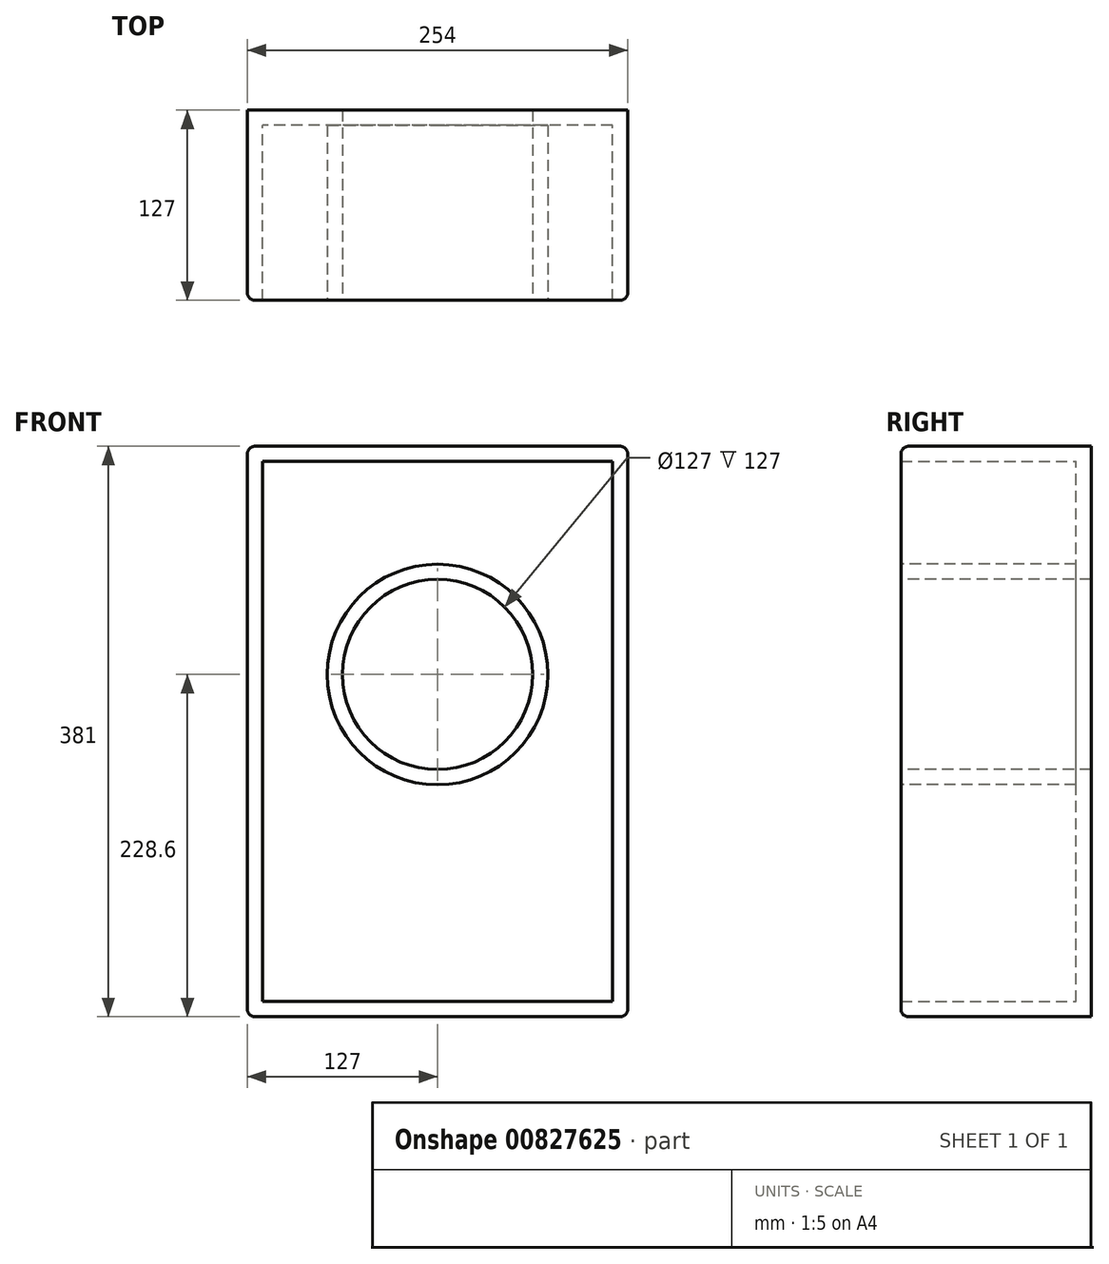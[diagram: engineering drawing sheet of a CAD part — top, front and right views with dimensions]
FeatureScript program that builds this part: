
annotation { "Feature Type Name" : "Feature", "Feature Type Description" : "" }
export const myFeature = defineFeature(function(context is Context, id is Id, definition is map)
    precondition{}
    {
        {
            var Q0;
            Q0=qCreatedBy(makeId("Front.planeOp"),FACE);
            var sketch = newSketch(context, id + "F0", { "sketchPlane" : qUnion([Q0])});
            skLineSegment(sketch, "E0.bottom", {"start": v(127, -190.5) * mm, "end": v(-127, -190.5) * mm});
            skLineSegment(sketch, "E0.top", {"start": v(127, 190.5) * mm, "end": v(-127, 190.5) * mm});
            skLineSegment(sketch, "E0.left", {"start": v(127, -190.5) * mm, "end": v(127, 190.5) * mm});
            skLineSegment(sketch, "E0.right", {"start": v(-127, -190.5) * mm, "end": v(-127, 190.5) * mm});
            skPoint(sketch, "E0.middle", {"position": v(0, 0) * mm});
            skSolve(sketch);
        }
        {
            var Q0;
            Q0=makeQuery(id+"F0.imprint","IMPRINT",FACE,{"disambiguationData":[TD([[makeQuery(id+"F0.imprint","IMPRINT",EDGE,{"derivedFrom":sQuery(id+"F0.wireOp",EDGE,"E0.bottom")}),-1.0]])]});
            extrude(context, id + "F1", {"entities" : qUnion([Q0]), "depth" : 127 * mm, "offsetDistance" : 25.4 * mm});
        }
        {
            var Q0;
            Q0=makeQuery(id+"F1.opExtrude","CAP_FACE",FACE,{"disambiguationData":[OSD([sQuery(id+"F0.wireOp",EDGE,"E0.bottom"),sQuery(id+"F0.wireOp",EDGE,"E0.top"),sQuery(id+"F0.wireOp",EDGE,"E0.left"),sQuery(id+"F0.wireOp",EDGE,"E0.right")])],"isStart":false});
            var sketch = newSketch(context, id + "F2", { "sketchPlane" : qUnion([Q0])});
            skCircle(sketch, "E1", {"center": v(0, 38.1) * mm, "radius": 63.5 * mm});
            skSolve(sketch);
        }
        {
            var Q0;
            Q0=makeQuery(id+"F2.imprint","IMPRINT",FACE,{"disambiguationData":[TD([[makeQuery(id+"F2.imprint","IMPRINT",EDGE,{"derivedFrom":sQuery(id+"F2.wireOp",EDGE,"E1")}),1.0]])]});
            var Q1;
            Q1=sQuery(id+"F2.wireOp",EDGE,"E1");
            extrude(context, id + "F3", {"entities" : qUnion([Q0]), "operationType" : NewBodyOperationType.REMOVE, "surfaceEntities" : qUnion([Q1]), "endBound" : BoundingType.THROUGH_ALL, "oppositeDirection" : true, "depth" : 25.4 * mm, "offsetDistance" : 25.4 * mm});
        }
        {
            var Q0;
            Q0=makeQuery(id+"F1.opExtrude","CAP_FACE",FACE,{"disambiguationData":[OSD([sQuery(id+"F0.wireOp",EDGE,"E0.bottom"),sQuery(id+"F0.wireOp",EDGE,"E0.top"),sQuery(id+"F0.wireOp",EDGE,"E0.left"),sQuery(id+"F0.wireOp",EDGE,"E0.right")])],"isStart":false});
            shell(context, id + "F4", {"entities" : qUnion([Q0]), "thickness" : 10.16 * mm});
        }
        {
            var Q0;
            Q0=makeQuery(id+"F1.opExtrude","CAP_EDGE",EDGE,{"disambiguationData":[OSD([sQuery(id+"F0.wireOp",EDGE,"E0.right")])],"isStart":false});
            var Q1;
            Q1=makeQuery(id+"F1.opExtrude","CAP_EDGE",EDGE,{"disambiguationData":[OSD([sQuery(id+"F0.wireOp",EDGE,"E0.top")])],"isStart":false});
            var Q2;
            Q2=makeQuery(id+"F1.opExtrude","CAP_EDGE",EDGE,{"disambiguationData":[OSD([sQuery(id+"F0.wireOp",EDGE,"E0.left")])],"isStart":false});
            var Q3;
            Q3=makeQuery(id+"F1.opExtrude","CAP_EDGE",EDGE,{"disambiguationData":[OSD([sQuery(id+"F0.wireOp",EDGE,"E0.bottom")])],"isStart":false});
            var Q4;
            Q4=makeQuery(id+"F1.opExtrude","SWEPT_EDGE",EDGE,{"disambiguationData":[OSD([sQuery(id+"F0.wireOp",EDGE,"E0.bottom"),sQuery(id+"F0.wireOp",EDGE,"E0.left")])]});
            var Q5;
            Q5=makeQuery(id+"F1.opExtrude","SWEPT_EDGE",EDGE,{"disambiguationData":[OSD([sQuery(id+"F0.wireOp",EDGE,"E0.top"),sQuery(id+"F0.wireOp",EDGE,"E0.left")])]});
            var Q6;
            Q6=makeQuery(id+"F1.opExtrude","SWEPT_EDGE",EDGE,{"disambiguationData":[OSD([sQuery(id+"F0.wireOp",EDGE,"E0.top"),sQuery(id+"F0.wireOp",EDGE,"E0.right")])]});
            var Q7;
            Q7=makeQuery(id+"F1.opExtrude","SWEPT_EDGE",EDGE,{"disambiguationData":[OSD([sQuery(id+"F0.wireOp",EDGE,"E0.bottom"),sQuery(id+"F0.wireOp",EDGE,"E0.right")])]});
            fillet(context, id + "F5", {"entities" : qUnion([Q0, Q1, Q2, Q3, Q4, Q5, Q6, Q7]), "radius" : 5.08 * mm, "tangentPropagation" : true, "allowEdgeOverflow" : false});
        }
    });
